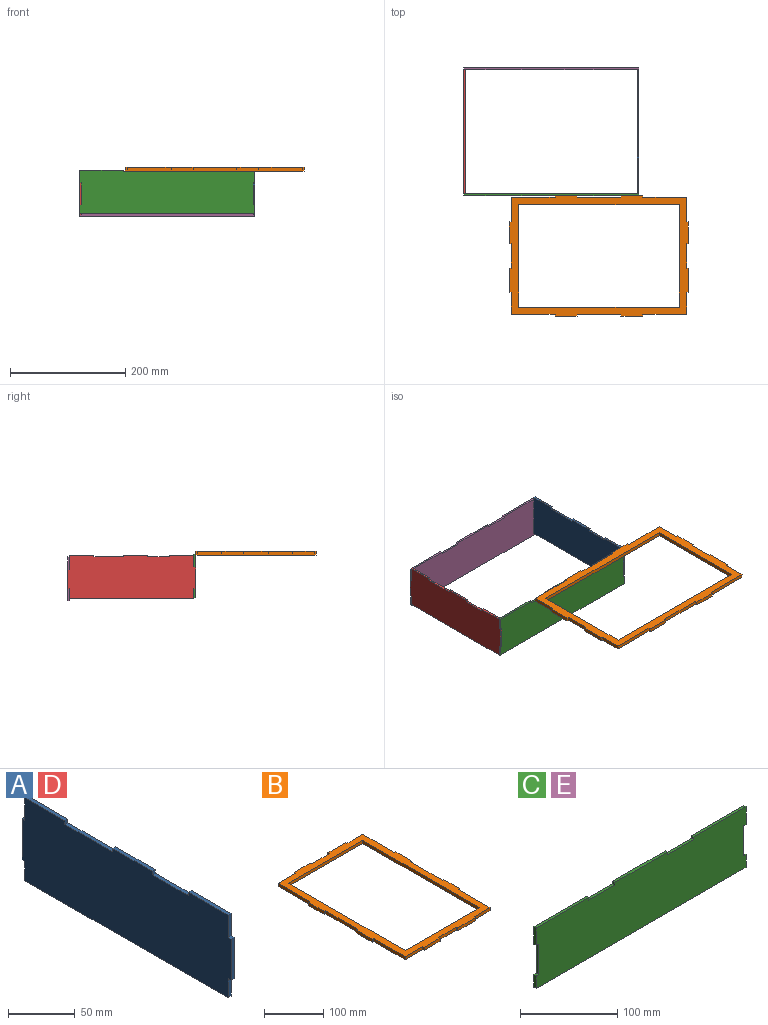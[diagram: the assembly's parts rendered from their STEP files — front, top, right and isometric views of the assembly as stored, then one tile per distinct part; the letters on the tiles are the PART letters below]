
ASSEMBLY  parts=5 mates=12
PART A: 22 faces, bbox 3.2x222.3x76.2 mm
  f0: plane 3.18x3.18mm, normal (0,0,-1), area 10.1mm2, adj f1,f19,f20,f21
  f1: plane 17.46x3.18mm, normal (0,-1,0), area 55.4mm2, adj f0,f2,f20,f21
  f2: plane 215.9x3.18mm, normal (0,0,-1), area 685.5mm2, adj f1,f3,f20,f21
  f3: plane 17.46x3.18mm, normal (0,1,0), area 55.4mm2, adj f2,f4,f20,f21
  f4: plane 3.18x3.18mm, normal (0,0,-1), area 10.1mm2, adj f3,f5,f20,f21
  f5: plane 38.1x3.18mm, normal (0,1,0), area 121mm2, adj f4,f6,f20,f21
  f6: plane 3.18x3.18mm, normal (0,0,1), area 10.1mm2, adj f5,f7,f20,f21
  f7: plane 20.64x3.18mm, normal (0,1,0), area 65.5mm2, adj f6,f8,f20,f21
  f8: plane 42.33x3.18mm, normal (0,0,1), area 134.4mm2, adj f7,f9,f20,f21
  f9: plane 3.18x3.18mm, normal (0,-1,0), area 10.1mm2, adj f8,f10,f20,f21
  f10: plane 50.8x3.18mm, normal (0,0,1), area 161.3mm2, adj f9,f11,f20,f21
  f11: plane 3.18x3.18mm, normal (0,1,0), area 10.1mm2, adj f10,f12,f20,f21
  f12: plane 42.33x3.18mm, normal (0,0,1), area 134.4mm2, adj f11,f13,f20,f21
  f13: plane 3.18x3.18mm, normal (0,-1,0), area 10.1mm2, adj f12,f14,f20,f21
  f14: plane 38.1x3.18mm, normal (0,0,1), area 121mm2, adj f13,f15,f20,f21
  f15: plane 3.18x3.18mm, normal (0,1,0), area 10.1mm2, adj f14,f16,f20,f21
  f16: plane 42.33x3.18mm, normal (0,0,1), area 134.4mm2, adj f15,f17,f20,f21
  f17: plane 20.64x3.18mm, normal (0,-1,0), area 65.5mm2, adj f16,f18,f20,f21
  f18: plane 3.18x3.18mm, normal (0,0,1), area 10.1mm2, adj f17,f19,f20,f21
  f19: plane 38.1x3.18mm, normal (0,-1,0), area 121mm2, adj f0,f18,f20,f21
  f20: plane 222.25x76.2mm, normal (-1,0,0), area 16411.3mm2, adj f0,f1,f2,f3,f4,f5,f6,f7
  f21: plane 222.25x76.2mm, normal (1,0,0), area 16411.3mm2, adj f0,f1,f2,f3,f4,f5,f6,f7
PART B: 42 faces, bbox 209.6x311.2x6.4 mm
  f0: plane 311.15x209.55mm, normal (0,0,-1), area 13252.7mm2, adj f2,f3,f4,f5,f6,f7,f8,f9
  f1: plane 311.15x209.55mm, normal (0,0,1), area 13252.7mm2, adj f2,f3,f4,f5,f6,f7,f8,f9
  f2: plane 76.2x6.35mm, normal (1,0,0), area 483.9mm2, adj f0,f1,f3,f37
  f3: plane 6.35x3.18mm, normal (0,-1,0), area 20.2mm2, adj f0,f1,f2,f4
  f4: plane 38.1x6.35mm, normal (1,0,0), area 241.9mm2, adj f0,f1,f3,f5
  f5: plane 6.35x3.18mm, normal (0,1,0), area 20.2mm2, adj f0,f1,f4,f6
  f6: plane 76.2x6.35mm, normal (1,0,0), area 483.9mm2, adj f0,f1,f5,f7
  f7: plane 6.35x3.18mm, normal (0,-1,0), area 20.2mm2, adj f0,f1,f6,f8
  f8: plane 38.1x6.35mm, normal (1,0,0), area 241.9mm2, adj f0,f1,f7,f9
  f9: plane 6.35x3.18mm, normal (0,1,0), area 20.2mm2, adj f0,f1,f8,f10
  f10: plane 76.2x6.35mm, normal (1,0,0), area 483.9mm2, adj f0,f1,f9,f11
  f11: plane 38.09x6.35mm, normal (0,1,0), area 241.9mm2, adj f0,f1,f10,f12
  f12: plane 6.35x3.18mm, normal (1,0,0), area 20.2mm2, adj f0,f1,f11,f13
  f13: plane 42.33x6.35mm, normal (0,1,0), area 268.8mm2, adj f0,f1,f12,f14
  f14: plane 6.35x3.18mm, normal (-1,0,0), area 20.2mm2, adj f0,f1,f13,f15
  f15: plane 42.34x6.35mm, normal (0,1,0), area 268.9mm2, adj f0,f1,f14,f16
  f16: plane 6.35x3.18mm, normal (1,0,0), area 20.2mm2, adj f0,f1,f15,f17
  f17: plane 38.1x6.35mm, normal (0,1,0), area 241.9mm2, adj f0,f1,f16,f18
  f18: plane 6.35x3.18mm, normal (-1,0,0), area 20.2mm2, adj f0,f1,f17,f19
  f19: plane 42.33x6.35mm, normal (0,1,0), area 268.8mm2, adj f0,f1,f18,f20
  f20: plane 76.2x6.35mm, normal (-1,0,0), area 483.9mm2, adj f0,f1,f19,f21
  f21: plane 6.35x3.18mm, normal (0,1,0), area 20.2mm2, adj f0,f1,f20,f22
  f22: plane 38.1x6.35mm, normal (-1,0,0), area 241.9mm2, adj f0,f1,f21,f23
  f23: plane 6.35x3.18mm, normal (0,-1,0), area 20.2mm2, adj f0,f1,f22,f24
  f24: plane 76.2x6.35mm, normal (-1,0,0), area 483.9mm2, adj f0,f1,f23,f25
  f25: plane 6.35x3.18mm, normal (0,1,0), area 20.2mm2, adj f0,f1,f24,f26
  f26: plane 38.1x6.35mm, normal (-1,0,0), area 241.9mm2, adj f0,f1,f25,f27
  f27: plane 6.35x3.18mm, normal (0,-1,0), area 20.2mm2, adj f0,f1,f26,f28
  f28: plane 76.2x6.35mm, normal (-1,0,0), area 483.9mm2, adj f0,f1,f27,f29
  f29: plane 42.33x6.35mm, normal (0,-1,0), area 268.8mm2, adj f0,f1,f28,f30
  f30: plane 6.35x3.18mm, normal (-1,0,0), area 20.2mm2, adj f0,f1,f29,f31
  f31: plane 38.1x6.35mm, normal (0,-1,0), area 241.9mm2, adj f0,f1,f30,f32
  f32: plane 6.35x3.18mm, normal (1,0,0), area 20.2mm2, adj f0,f1,f31,f33
  f33: plane 42.34x6.35mm, normal (0,-1,0), area 268.9mm2, adj f0,f1,f32,f34
  f34: plane 6.35x3.18mm, normal (-1,0,0), area 20.2mm2, adj f0,f1,f33,f35
  f35: plane 42.33x6.35mm, normal (0,-1,0), area 268.8mm2, adj f0,f1,f34,f36
  f36: plane 6.35x3.18mm, normal (1,0,0), area 20.2mm2, adj f0,f1,f35,f37
  f37: plane 38.09x6.35mm, normal (0,-1,0), area 241.9mm2, adj f0,f1,f2,f36
  f38: plane 177.8x6.35mm, normal (0,-1,0), area 1129mm2, adj f0,f1,f39,f41
  f39: plane 279.4x6.35mm, normal (1,0,0), area 1774.2mm2, adj f0,f1,f38,f40
  f40: plane 177.8x6.35mm, normal (0,1,0), area 1129mm2, adj f0,f1,f39,f41
  f41: plane 279.4x6.35mm, normal (-1,0,0), area 1774.2mm2, adj f0,f1,f38,f40
PART C: 22 faces, bbox 304.8x3.2x76.2 mm
  f0: plane 22.23x3.18mm, normal (-1,0,0), area 70.6mm2, adj f1,f19,f20,f21
  f1: plane 3.18x3.18mm, normal (0,0,-1), area 10.1mm2, adj f0,f2,f20,f21
  f2: plane 38.1x3.18mm, normal (-1,0,0), area 121mm2, adj f1,f3,f20,f21
  f3: plane 3.18x3.18mm, normal (0,0,1), area 10.1mm2, adj f2,f4,f20,f21
  f4: plane 15.88x3.18mm, normal (-1,0,0), area 50.4mm2, adj f3,f5,f20,f21
  f5: plane 304.8x3.18mm, normal (0,0,-1), area 967.7mm2, adj f4,f6,f20,f21
  f6: plane 15.88x3.18mm, normal (1,0,0), area 50.4mm2, adj f5,f7,f20,f21
  f7: plane 3.18x3.18mm, normal (0,0,1), area 10.1mm2, adj f6,f8,f20,f21
  f8: plane 38.1x3.18mm, normal (1,0,0), area 121mm2, adj f7,f9,f20,f21
  f9: plane 3.18x3.18mm, normal (0,0,-1), area 10.1mm2, adj f8,f10,f20,f21
  f10: plane 22.23x3.18mm, normal (1,0,0), area 70.6mm2, adj f9,f11,f20,f21
  f11: plane 76.2x3.18mm, normal (0,0,1), area 241.9mm2, adj f10,f12,f20,f21
  f12: plane 3.18x3.18mm, normal (-1,0,0), area 10.1mm2, adj f11,f13,f20,f21
  f13: plane 38.1x3.18mm, normal (0,0,1), area 121mm2, adj f12,f14,f20,f21
  f14: plane 3.18x3.18mm, normal (1,0,0), area 10.1mm2, adj f13,f15,f20,f21
  f15: plane 76.2x3.18mm, normal (0,0,1), area 241.9mm2, adj f14,f16,f20,f21
  f16: plane 3.18x3.18mm, normal (-1,0,0), area 10.1mm2, adj f15,f17,f20,f21
  f17: plane 38.1x3.18mm, normal (0,0,1), area 121mm2, adj f16,f18,f20,f21
  f18: plane 3.18x3.18mm, normal (1,0,0), area 10.1mm2, adj f17,f19,f20,f21
  f19: plane 76.2x3.18mm, normal (0,0,1), area 241.9mm2, adj f0,f18,f20,f21
  f20: plane 304.8x76.2mm, normal (0,-1,0), area 22741.9mm2, adj f0,f1,f2,f3,f4,f5,f6,f7
  f21: plane 304.8x76.2mm, normal (0,1,0), area 22741.9mm2, adj f0,f1,f2,f3,f4,f5,f6,f7
PART D: same geometry as A
PART E: same geometry as C
PLACE A t=(135.28,265.53,291.26)mm
PLACE B rot(axis=(0,0,-1),90deg) t=(65.79,49.63,337.3)mm
PLACE C rot(axis=(-0.19,0.97,0.14),0deg) t=(-11.97,157.58,305.03)mm
PLACE D t=(-166.35,265.53,291.26)mm
PLACE E t=(-11.97,376.65,300.49)mm
MATE planar D.f20 <-> C.f4  axis (-1,0,0) through (-169.52,265.47,292.2)mm
MATE planar D.f5 <-> E.f21  axis (0,1,0) through (-167.93,376.65,291.26)mm
MATE planar D.f17 <-> C.f21  axis (0,-1,0) through (-167.93,157.58,320.63)mm
MATE planar B.f8 <-> E.f21  axis (0,-1,0) through (122.94,-55.15,334.13)mm
MATE planar B.f26 <-> C.f20  axis (0,1,0) through (8.64,154.4,334.13)mm
MATE planar E.f8 <-> A.f20  axis (1,0,0) through (132.1,375.06,286.73)mm
MATE planar E.f21 <-> A.f5  axis (0,1,0) through (132.1,376.65,286.73)mm
MATE planar D.f19 <-> C.f20  axis (0,-1,0) through (-167.93,154.4,291.26)mm
MATE planar A.f21 <-> C.f10  axis (1,0,0) through (135.28,157.58,272.21)mm
MATE planar B.f0 <-> A.f8  axis (0,0,-1) through (8.64,-55.15,330.95)mm
MATE planar D.f18 <-> C.f1  axis (0,0,1) through (-167.93,155.99,310.31)mm
MATE planar A.f0 <-> C.f7  axis (0,0,-1) through (133.69,155.99,272.21)mm
